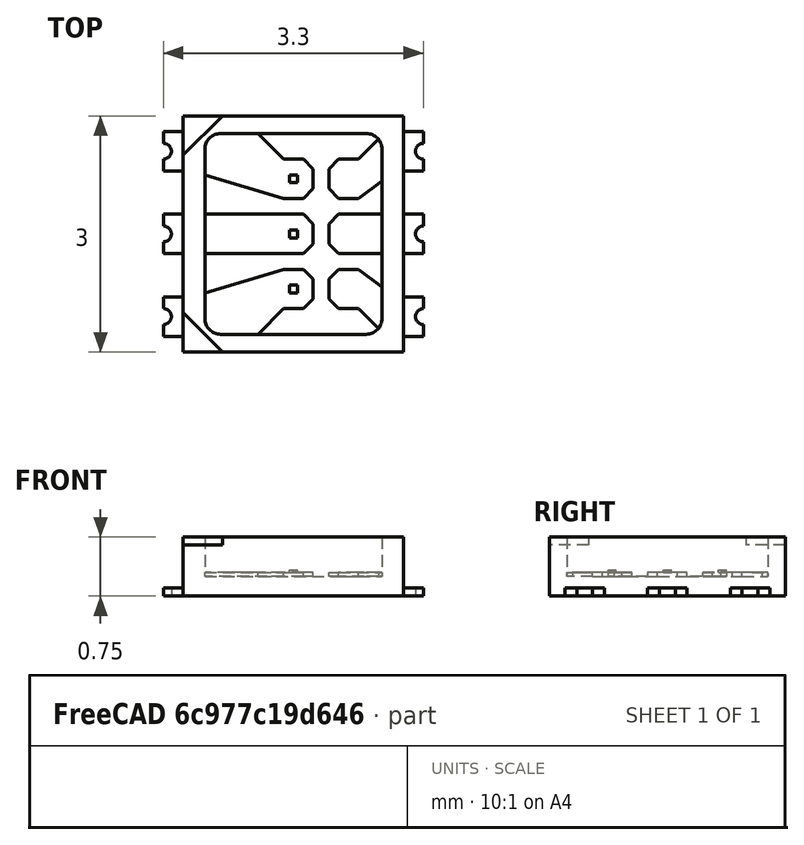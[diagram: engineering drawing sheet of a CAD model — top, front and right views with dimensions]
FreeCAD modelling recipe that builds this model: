
FCSTD DOCUMENT  (FreeCAD 0.17R11740 (Git)/Daily-PPA)
Label: LED_NSSM124_footprinthelper
License: All rights reserved
LicenseURL: http://en.wikipedia.org/wiki/All_rights_reserved
objects: Sketcher::SketchObject×2, Part::Feature×1
note: 3 computed .brp shape members not serialized (recipe doc carries the construction recipe); baked Part::Feature solids carry a one-line shape summary decoded from their .brp

FEATURE [Part::Feature] Fusion001  label="LED_NSSM124_simple"
  shape: bbox 3.3 x 3 x 0.75 mm, 126 faces (baked)
FEATURE [Sketcher::SketchObject] Sketch  label="footprint_basic"
  MapMode = 5
  sketch-geometry (30):
    g0: LineSegment StartX=-2.25 StartY=1.525 StartZ=0 EndX=-1.1 EndY=1.525 EndZ=0
    g1: LineSegment StartX=-1.1 StartY=1.525 StartZ=0 EndX=-1.1 EndY=0.675 EndZ=0
    g2: LineSegment StartX=-1.1 StartY=0.675 StartZ=0 EndX=-2.25 EndY=0.675 EndZ=0
    g3: LineSegment StartX=-2.25 StartY=0.675 StartZ=0 EndX=-2.25 EndY=1.525 EndZ=0
    g4: LineSegment StartX=-2.25 StartY=0.375 StartZ=0 EndX=-1.1 EndY=0.375 EndZ=0
    g5: LineSegment StartX=-1.1 StartY=0.375 StartZ=0 EndX=-1.1 EndY=-0.375 EndZ=0
    g6: LineSegment StartX=-1.1 StartY=-0.375 StartZ=0 EndX=-2.25 EndY=-0.375 EndZ=0
    g7: LineSegment StartX=-2.25 StartY=-0.375 StartZ=0 EndX=-2.25 EndY=0.375 EndZ=0
    g8: LineSegment StartX=-2.25 StartY=-0.675 StartZ=0 EndX=-1.1 EndY=-0.675 EndZ=0
    g9: LineSegment StartX=-1.1 StartY=-0.675 StartZ=0 EndX=-1.1 EndY=-1.525 EndZ=0
    g10: LineSegment StartX=-1.1 StartY=-1.525 StartZ=0 EndX=-2.25 EndY=-1.525 EndZ=0
    g11: LineSegment StartX=-2.25 StartY=-1.525 StartZ=0 EndX=-2.25 EndY=-0.675 EndZ=0
    g12: LineSegment [constr] StartX=-2.25 StartY=-0.375 StartZ=0 EndX=-2.25 EndY=-0.675 EndZ=0
    g13: LineSegment [constr] StartX=-2.25 StartY=0.675 StartZ=0 EndX=-2.25 EndY=0.375 EndZ=0
    g14: LineSegment StartX=2.25 StartY=1.525 StartZ=0 EndX=1.1 EndY=1.525 EndZ=0
    g15: LineSegment StartX=1.1 StartY=1.525 StartZ=0 EndX=1.1 EndY=0.675 EndZ=0
    g16: LineSegment StartX=1.1 StartY=0.675 StartZ=0 EndX=2.25 EndY=0.675 EndZ=0
    g17: LineSegment StartX=2.25 StartY=0.675 StartZ=0 EndX=2.25 EndY=1.525 EndZ=0
    g18: LineSegment StartX=2.25 StartY=0.375 StartZ=0 EndX=1.1 EndY=0.375 EndZ=0
    g19: LineSegment StartX=1.1 StartY=0.375 StartZ=0 EndX=1.1 EndY=-0.375 EndZ=0
    g20: LineSegment StartX=1.1 StartY=-0.375 StartZ=0 EndX=2.25 EndY=-0.375 EndZ=0
    g21: LineSegment StartX=2.25 StartY=-0.375 StartZ=0 EndX=2.25 EndY=0.375 EndZ=0
    g22: LineSegment StartX=2.25 StartY=-0.675 StartZ=0 EndX=1.1 EndY=-0.675 EndZ=0
    g23: LineSegment StartX=1.1 StartY=-0.675 StartZ=0 EndX=1.1 EndY=-1.525 EndZ=0
    g24: LineSegment StartX=1.1 StartY=-1.525 StartZ=0 EndX=2.25 EndY=-1.525 EndZ=0
    g25: LineSegment StartX=2.25 StartY=-1.525 StartZ=0 EndX=2.25 EndY=-0.675 EndZ=0
    g26: LineSegment [constr] StartX=2.25 StartY=-0.375 StartZ=0 EndX=2.25 EndY=-0.675 EndZ=0
    g27: LineSegment [constr] StartX=2.25 StartY=0.675 StartZ=0 EndX=2.25 EndY=0.375 EndZ=0
    g28: LineSegment [constr] StartX=-1.1 StartY=0 StartZ=0 EndX=1.1 EndY=0 EndZ=0
    g29: GeomPoint X=-1.675 Y=-1.1 Z=0
  constraints (86):
    c: Coincident(g0,g1)
    c: Coincident(g1,g2)
    c: Coincident(g2,g3)
    c: Coincident(g3,g0)
    c: Horizontal(g0)
    c: Horizontal(g2)
    c: Vertical(g1)
    c: Vertical(g3)
    c: DistanceX(g0,g0) = 1.15  'pad_width'
    c: DistanceY(g3,g3) = 0.85  'pad_height_out'
    c: Coincident(g4,g5)
    c: Coincident(g5,g6)
    c: Coincident(g6,g7)
    c: Coincident(g7,g4)
    c: Horizontal(g4)
    c: Horizontal(g6)
    c: Vertical(g5)
    c: Vertical(g7)
    c: Coincident(g8,g9)
    c: Coincident(g9,g10)
    c: Coincident(g10,g11)
    c: Coincident(g11,g8)
    c: Horizontal(g8)
    c: Horizontal(g10)
    c: Vertical(g9)
    c: Vertical(g11)
    c: DistanceY(g7,g7) = 0.75  'pad_height_in'
    c: Equal(g11,g3)
    c: Equal(g8,g4)
    c: Equal(g4,g0)
    c: DistanceY(g10,g0) = 3.05
    c: Coincident(g8,g12)
    c: Coincident(g6,g12)
    c: Vertical(g12)
    c: Coincident(g4,g13)
    c: Coincident(g2,g13)
    c: Vertical(g13)
    c: Equal(g13,g12)
    c: Coincident(g14,g15)
    c: Coincident(g15,g16)
    c: Coincident(g16,g17)
    c: Coincident(g17,g14)
    c: Horizontal(g14)
    c: Horizontal(g16)
    c: Vertical(g15)
    c: Vertical(g17)
    c: Coincident(g18,g19)
    c: Coincident(g19,g20)
    c: Coincident(g20,g21)
    c: Coincident(g21,g18)
    c: Horizontal(g18)
    c: Horizontal(g20)
    c: Vertical(g19)
    c: Vertical(g21)
    c: Coincident(g22,g23)
    c: Coincident(g23,g24)
    c: Coincident(g24,g25)
    c: Coincident(g25,g22)
    c: Horizontal(g22)
    c: Horizontal(g24)
    c: Vertical(g23)
    c: Vertical(g25)
    c: Equal(g25,g17)
    c: Equal(g22,g18)
    c: Equal(g18,g14)
    c: Coincident(g22,g26)
    c: Coincident(g20,g26)
    c: Vertical(g26)
    c: Coincident(g18,g27)
    c: Coincident(g16,g27)
    c: Vertical(g27)
    c: Equal(g27,g26)
    c: PointOnObject(g23,g10)
    c: PointOnObject(g14,g0)
    c: Equal(g17,g3)
    c: Equal(g14,g0)
    c: Equal(g21,g7)
    c: Horizontal(g28)
    c: Symmetric(g28,g28,g-1)
    c: Symmetric(g19,g19,g28)
    c: Symmetric(g5,g5,g28)
    c: DistanceX(g0,g14) = 4.5
    c: DistanceX(g0,g14) = 2.2
    c: Symmetric(g8,g10,g29)
    c: DistanceX(g29) = -1.675
    c: DistanceY(g29) = -1.1
FEATURE [Sketcher::SketchObject] Sketch001  label="footprint_wViaHeatSink"
  MapMode = 5
  sketch-geometry (39):
    g0: LineSegment StartX=-2.25 StartY=1.525 StartZ=0 EndX=0.75 EndY=1.525 EndZ=0
    g1: LineSegment StartX=0.75 StartY=1.525 StartZ=0 EndX=0.75 EndY=0.675 EndZ=0
    g2: LineSegment StartX=0.75 StartY=0.675 StartZ=0 EndX=-2.25 EndY=0.675 EndZ=0
    g3: LineSegment StartX=-2.25 StartY=0.675 StartZ=0 EndX=-2.25 EndY=1.525 EndZ=0
    g4: LineSegment StartX=-2.25 StartY=0.375 StartZ=0 EndX=0.75 EndY=0.375 EndZ=0
    g5: LineSegment StartX=0.75 StartY=0.375 StartZ=0 EndX=0.75 EndY=-0.375 EndZ=0
    g6: LineSegment StartX=0.75 StartY=-0.375 StartZ=0 EndX=-2.25 EndY=-0.375 EndZ=0
    g7: LineSegment StartX=-2.25 StartY=-0.375 StartZ=0 EndX=-2.25 EndY=0.375 EndZ=0
    g8: LineSegment StartX=-2.25 StartY=-0.675 StartZ=0 EndX=0.75 EndY=-0.675 EndZ=0
    g9: LineSegment StartX=0.75 StartY=-0.675 StartZ=0 EndX=0.75 EndY=-1.525 EndZ=0
    g10: LineSegment StartX=0.75 StartY=-1.525 StartZ=0 EndX=-2.25 EndY=-1.525 EndZ=0
    g11: LineSegment StartX=-2.25 StartY=-1.525 StartZ=0 EndX=-2.25 EndY=-0.675 EndZ=0
    g12: LineSegment [constr] StartX=-2.25 StartY=-0.375 StartZ=0 EndX=-2.25 EndY=-0.675 EndZ=0
    g13: LineSegment [constr] StartX=-2.25 StartY=0.675 StartZ=0 EndX=-2.25 EndY=0.375 EndZ=0
    g14: LineSegment StartX=2.25 StartY=1.525 StartZ=0 EndX=1.1 EndY=1.525 EndZ=0
    g15: LineSegment StartX=1.1 StartY=1.525 StartZ=0 EndX=1.1 EndY=0.675 EndZ=0
    g16: LineSegment StartX=1.1 StartY=0.675 StartZ=0 EndX=2.25 EndY=0.675 EndZ=0
    g17: LineSegment StartX=2.25 StartY=0.675 StartZ=0 EndX=2.25 EndY=1.525 EndZ=0
    g18: LineSegment StartX=2.25 StartY=0.375 StartZ=0 EndX=1.1 EndY=0.375 EndZ=0
    g19: LineSegment StartX=1.1 StartY=0.375 StartZ=0 EndX=1.1 EndY=-0.375 EndZ=0
    g20: LineSegment StartX=1.1 StartY=-0.375 StartZ=0 EndX=2.25 EndY=-0.375 EndZ=0
    g21: LineSegment StartX=2.25 StartY=-0.375 StartZ=0 EndX=2.25 EndY=0.375 EndZ=0
    g22: LineSegment StartX=2.25 StartY=-0.675 StartZ=0 EndX=1.1 EndY=-0.675 EndZ=0
    g23: LineSegment StartX=1.1 StartY=-0.675 StartZ=0 EndX=1.1 EndY=-1.525 EndZ=0
    g24: LineSegment StartX=1.1 StartY=-1.525 StartZ=0 EndX=2.25 EndY=-1.525 EndZ=0
    g25: LineSegment StartX=2.25 StartY=-1.525 StartZ=0 EndX=2.25 EndY=-0.675 EndZ=0
    g26: LineSegment [constr] StartX=2.25 StartY=-0.375 StartZ=0 EndX=2.25 EndY=-0.675 EndZ=0
    g27: LineSegment [constr] StartX=2.25 StartY=0.675 StartZ=0 EndX=2.25 EndY=0.375 EndZ=0
    g28: GeomPoint X=-0.75 Y=-1.1 Z=0
    g29: GeomPoint X=1.675 Y=-1.1 Z=0
    g30: GeomPoint X=1.675 Y=0 Z=0
    g31: LineSegment StartX=-1.65 StartY=1.5 StartZ=0 EndX=1.65 EndY=1.5 EndZ=0
    g32: LineSegment StartX=1.65 StartY=1.5 StartZ=0 EndX=1.65 EndY=-1.5 EndZ=0
    g33: LineSegment StartX=1.65 StartY=-1.5 StartZ=0 EndX=-1.65 EndY=-1.5 EndZ=0
    g34: LineSegment StartX=-1.65 StartY=-1.5 StartZ=0 EndX=-1.65 EndY=1.5 EndZ=0
    g35: LineSegment StartX=-2.5 StartY=1.775 StartZ=0 EndX=2.5 EndY=1.775 EndZ=0
    g36: LineSegment StartX=2.5 StartY=1.775 StartZ=0 EndX=2.5 EndY=-1.775 EndZ=0
    g37: LineSegment StartX=2.5 StartY=-1.775 StartZ=0 EndX=-2.5 EndY=-1.775 EndZ=0
    g38: LineSegment StartX=-2.5 StartY=-1.775 StartZ=0 EndX=-2.5 EndY=1.775 EndZ=0
  constraints (112):
    c: Coincident(g0,g1)
    c: Coincident(g1,g2)
    c: Coincident(g2,g3)
    c: Coincident(g3,g0)
    c: Horizontal(g0)
    c: Horizontal(g2)
    c: Vertical(g1)
    c: Vertical(g3)
    c: DistanceX(g0,g0) = 3  'pad_width'
    c: DistanceY(g3,g3) = 0.85  'pad_height_out'
    c: Coincident(g4,g5)
    c: Coincident(g5,g6)
    c: Coincident(g6,g7)
    c: Coincident(g7,g4)
    c: Horizontal(g4)
    c: Horizontal(g6)
    c: Vertical(g5)
    c: Vertical(g7)
    c: Coincident(g8,g9)
    c: Coincident(g9,g10)
    c: Coincident(g10,g11)
    c: Coincident(g11,g8)
    c: Horizontal(g8)
    c: Horizontal(g10)
    c: Vertical(g9)
    c: Vertical(g11)
    c: DistanceY(g7,g7) = 0.75  'pad_height_in'
    c: Equal(g11,g3)
    c: Equal(g8,g4)
    c: Equal(g4,g0)
    c: DistanceY(g10,g0) = 3.05
    c: Coincident(g8,g12)
    c: Coincident(g6,g12)
    c: Vertical(g12)
    c: Coincident(g4,g13)
    c: Coincident(g2,g13)
    c: Vertical(g13)
    c: Equal(g13,g12)
    c: Coincident(g14,g15)
    c: Coincident(g15,g16)
    c: Coincident(g16,g17)
    c: Coincident(g17,g14)
    c: Horizontal(g14)
    c: Horizontal(g16)
    c: Vertical(g15)
    c: Vertical(g17)
    c: Coincident(g18,g19)
    c: Coincident(g19,g20)
    c: Coincident(g20,g21)
    c: Coincident(g21,g18)
    c: Horizontal(g18)
    c: Horizontal(g20)
    c: Vertical(g19)
    c: Vertical(g21)
    c: Coincident(g22,g23)
    c: Coincident(g23,g24)
    c: Coincident(g24,g25)
    c: Coincident(g25,g22)
    c: Horizontal(g22)
    c: Horizontal(g24)
    c: Vertical(g23)
    c: Vertical(g25)
    c: Equal(g25,g17)
    c: Equal(g22,g18)
    c: Equal(g18,g14)
    c: Coincident(g22,g26)
    c: Coincident(g20,g26)
    c: Vertical(g26)
    c: Coincident(g18,g27)
    c: Coincident(g16,g27)
    c: Vertical(g27)
    c: Equal(g27,g26)
    c: PointOnObject(g23,g10)
    c: PointOnObject(g14,g0)
    c: Equal(g17,g3)
    c: Equal(g21,g7)
    c: DistanceX(g0,g14) = 4.5
    c: Symmetric(g8,g10,g28)
    c: DistanceX(g28) = -0.75
    c: DistanceY(g28) = -1.1
    c: DistanceX(g14,g14) = 1.15
    c: Symmetric(g23,g22,g29)
    c: DistanceX(g-1,g29) = 1.675
    c: Symmetric(g19,g18,g30)
    c: PointOnObject(g30,g-1)
    c: DistanceX(g0,g14) = 0.35
    c: DistanceX(g-1,g14) = 1.1
    c: Coincident(g31,g32)
    c: Coincident(g32,g33)
    c: Coincident(g33,g34)
    c: Coincident(g34,g31)
    c: Horizontal(g31)
    c: Horizontal(g33)
    c: Vertical(g32)
    c: Vertical(g34)
    c: Symmetric(g33,g31,g-1)
    c: DistanceY(g32,g32) = 3
    c: DistanceX(g33,g33) = 3.3
    c: Coincident(g35,g36)
    c: Coincident(g36,g37)
    c: Coincident(g37,g38)
    c: Coincident(g38,g35)
    c: Horizontal(g35)
    c: Horizontal(g37)
    c: Vertical(g36)
    c: Vertical(g38)
    c: DistanceX(g24,g36) = 0.25
    c: DistanceY(g36,g24) = 0.25
    c: Symmetric(g37,g35,g-1)
    c: DistanceX(g36) = 2.5
    c: DistanceY(g36) = -1.775
    c: DistanceY(g36,g36) = 3.55
